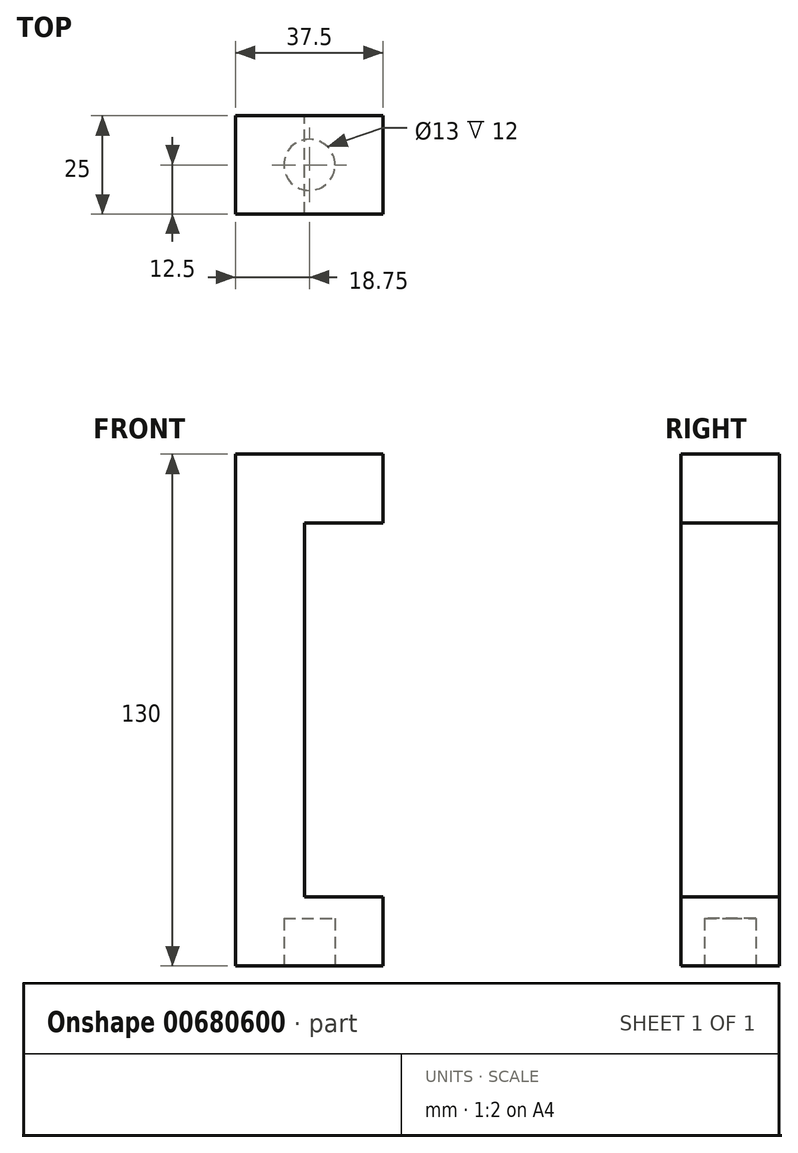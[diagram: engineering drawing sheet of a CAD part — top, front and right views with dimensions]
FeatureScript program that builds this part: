
annotation { "Feature Type Name" : "Feature", "Feature Type Description" : "" }
export const myFeature = defineFeature(function(context is Context, id is Id, definition is map)
    precondition{}
    {
        {
            var Q0;
            Q0=qCreatedBy(makeId("Front.planeOp"),FACE);
            var sketch = newSketch(context, id + "F0", { "sketchPlane" : qUnion([Q0])});
            skLineSegment(sketch, "E0", {"start": v(0, 0) * mm, "end": v(0, 65) * mm});
            skLineSegment(sketch, "E1", {"start": v(0, 65) * mm, "end": v(37.5, 65) * mm});
            skLineSegment(sketch, "E2", {"start": v(37.5, 65) * mm, "end": v(37.5, 47.5) * mm});
            skLineSegment(sketch, "E3", {"start": v(37.5, 47.5) * mm, "end": v(17.5, 47.5) * mm});
            skLineSegment(sketch, "E4", {"start": v(17.5, 47.5) * mm, "end": v(17.5, 0) * mm});
            skLineSegment(sketch, "E5", {"start": v(17.5, 0) * mm, "end": v(0, 0) * mm, "construction": true});
            skLineSegment(sketch, "E6", {"start": v(17.5, 47.5) * mm, "end": v(0, 47.5) * mm, "construction": true});
            skLineSegment(sketch, "E7", {"start": v(17.5, 47.5) * mm, "end": v(17.5, 65) * mm, "construction": true});
            skLineSegment(sketch, "E8.MirrorCS", {"start": v(0, 0) * mm, "end": v(0, -65) * mm});
            skLineSegment(sketch, "E9.MirrorCS", {"start": v(0, -65) * mm, "end": v(37.5, -65) * mm});
            skLineSegment(sketch, "E10.MirrorCS", {"start": v(17.5, -47.5) * mm, "end": v(17.5, -65) * mm, "construction": true});
            skLineSegment(sketch, "E11.MirrorCS", {"start": v(17.5, -47.5) * mm, "end": v(0, -47.5) * mm, "construction": true});
            skLineSegment(sketch, "E12.MirrorCS", {"start": v(17.5, -47.5) * mm, "end": v(17.5, 0) * mm});
            skLineSegment(sketch, "E13.MirrorCS", {"start": v(37.5, -47.5) * mm, "end": v(17.5, -47.5) * mm});
            skLineSegment(sketch, "E14.MirrorCS", {"start": v(37.5, -65) * mm, "end": v(37.5, -47.5) * mm});
            skSolve(sketch);
        }
        {
            var Q0;
            Q0 = qSketchRegion(id + "F0", true);
            extrude(context, id + "F1", {"entities" : qUnion([Q0]), "depth" : 12.5 * mm, "offsetDistance" : 25 * mm, "hasSecondDirection" : true, "secondDirectionOppositeDirection" : true, "secondDirectionDepth" : 12.5 * mm});
        }
        {
            var Q0;
            Q0=makeQuery(id+"F1.opExtrude","SWEPT_FACE",FACE,{"disambiguationData":[OSD([sQuery(id+"F0.wireOp",EDGE,"E9.MirrorCS")])]});
            var sketch = newSketch(context, id + "F2", { "sketchPlane" : qUnion([Q0])});
            skLineSegment(sketch, "E15", {"start": v(18.75, 12.5) * mm, "end": v(18.75, -12.5) * mm, "construction": true});
            skLineSegment(sketch, "E16", {"start": v(0, 0) * mm, "end": v(37.5, 0) * mm, "construction": true});
            skCircle(sketch, "E17", {"center": v(18.75, 0) * mm, "radius": 6.5 * mm});
            skSolve(sketch);
        }
        {
            var Q0;
            Q0 = qSketchRegion(id + "F2", true);
            extrude(context, id + "F3", {"entities" : qUnion([Q0]), "operationType" : NewBodyOperationType.REMOVE, "oppositeDirection" : true, "depth" : 12 * mm, "offsetDistance" : 25 * mm});
        }
    });
